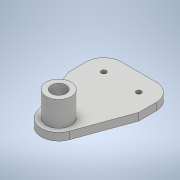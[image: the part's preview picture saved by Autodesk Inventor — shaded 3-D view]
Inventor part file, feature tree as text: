
AUTODESK INVENTOR PART (.ipt)
format: ipt  version: 2020 (Build 240168000, 168)  size: 139,776 bytes
history: native  units: mm
features: sketch x3, extrude x2, other x1, fillet x1, hole x1
ambient origin geometry x8: Origin, YZ Plane, XZ Plane, XY Plane, X Axis, Y Axis, Z Axis, Center Point
bodies: Body1 (feature_tree)
feature tree (8):
  other  "Твердое тело1"
  extrude  "Выдавливание1"  Depth=14.0mm
  extrude  "Выдавливание11"  Depth=7.0mm
  fillet  "Сопряжение1"  Radius=9.0mm
  hole  "Отверстие1"  [1 undecoded]
  sketch  "Эскиз1"
  sketch  "Эскиз2"
  sketch  "Эскиз5"
note: 1 required parameter value undecoded (feature->parameter linkage not recoverable at this tier; creation-order binding heuristic only, values carry confidence <= 0.55)
